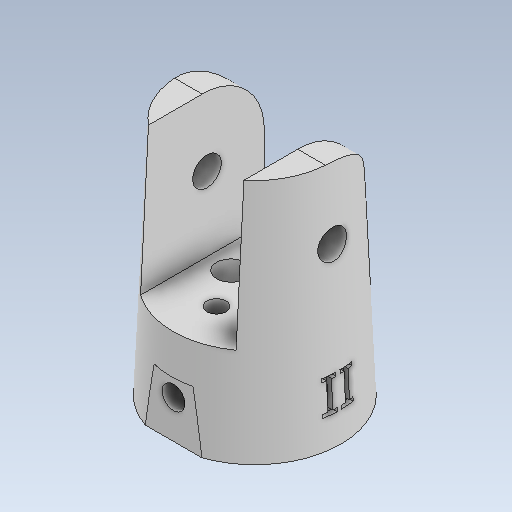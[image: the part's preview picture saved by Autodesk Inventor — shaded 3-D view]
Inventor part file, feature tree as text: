
AUTODESK INVENTOR PART (.ipt)
format: ipt  version: 2021 (Build 250183000, 183)  size: 272,896 bytes
history: native  units: mm
features: sketch x9, extrude x8, other x7, plane x2, fillet x1
ambient origin geometry x8: Origin, YZ Plane, XZ Plane, XY Plane, X Axis, Y Axis, Z Axis, Center Point
bodies: Volumenkörper1 (feature_tree), Volumenkörper5 (feature_tree), Volumenkörper7 (feature_tree), Volumenkörper8 (feature_tree), Volumenkörper9 (feature_tree), Volumenkörper10 (feature_tree)
feature tree (27):
  extrude  "Extrusion1"  Depth=25.0mm TaperAngle=0.0deg
  other  "Flächenverjüngung1"
  extrude  "Extrusion2"  Depth=10.0mm
  extrude  "Extrusion3"  Depth=3.0mm
  extrude  "Extrusion9"  Depth=30.0mm TaperAngle=0.0deg
  fillet  "Rundung3"  Radius=6.5mm
  other  "Kombinieren2"
  extrude  "Extrusion10"  Depth=6.0mm
  other  "Kombinieren4"
  extrude  "Extrusion11"  Depth=8.5mm TaperAngle=0.0deg
  other  "Kombinieren5"
  plane  "Arbeitsebene1"
  extrude  "Extrusion12"  Depth=6.0mm
  other  "Kombinieren6"
  extrude  "Extrusion13"  Depth=2.0mm
  other  "Kombinieren7"
  plane  "Arbeitsebene2"
  other  "Prägen1"
  sketch  "Skizze1"  dims[d6=18.0mm d7=25.0mm d8=0.0mm]
  sketch  "Skizze2"  dims[d12=15.0mm d13=0.0mm d14=10.0mm]
  sketch  "Skizze3"  dims[d15=5.0mm d16=3.0mm]
  sketch  "Skizze5"  dims[d18=30.0mm d19=0.0mm d42=30.0mm d43=0.0mm d44=6.5mm]
  sketch  "Skizze7"  dims[d46=7.25mm d47=6.0mm]
  sketch  "Skizze8"  dims[d48=8.5mm d49=40.0mm d50=0.0mm]
  sketch  "Skizze9"  dims[d51=-0.436332mm d52=6.0mm]
  sketch  "Skizze11"  dims[d53=0.0mm d55=2.0mm]
  sketch  "Skizze12"  dims[d56=22.25mm d57=0.0mm d58=5.5mm d60=2.4mm d61=4.0mm d63=22.25mm d64=0.0mm d66=0.0mm d68=15.0mm d69=0.0mm d70=3.0mm d71=3.0mm d72=2.5mm d73=0.0mm d74=2.5mm d75=0.0mm d76=4.0mm d77=9.0mm d78=3.5mm d79=3.5mm d80=1.8mm d81=0.5mm d82=0.0mm d83=3.0mm d17=0.872665mm d37=0.5mm d38=0.872665mm d39=0.5mm d40=0.872665mm d59=0.872665mm]
